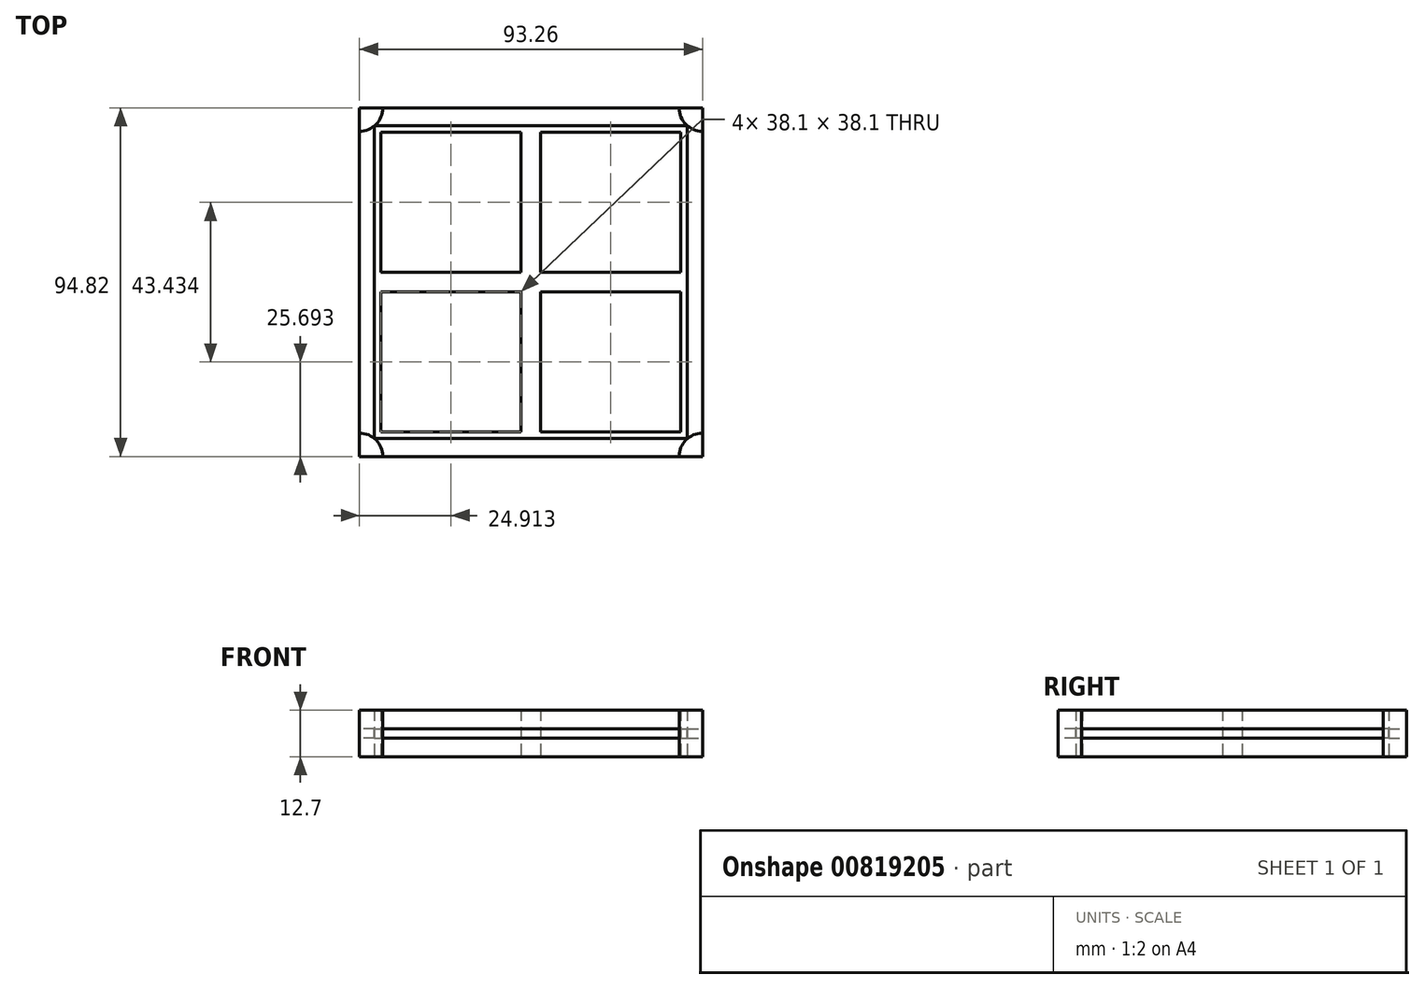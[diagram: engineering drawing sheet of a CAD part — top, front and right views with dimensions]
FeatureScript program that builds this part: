
annotation { "Feature Type Name" : "Feature", "Feature Type Description" : "" }
export const myFeature = defineFeature(function(context is Context, id is Id, definition is map)
    precondition{}
    {
        {
            var Q0;
            Q0=qCreatedBy(makeId("Top.planeOp"),FACE);
            var sketch = newSketch(context, id + "F0", { "sketchPlane" : qUnion([Q0])});
            skLineSegment(sketch, "E0.bottom", {"start": v(-42.55, 42.55) * mm, "end": v(42.55, 42.55) * mm});
            skLineSegment(sketch, "E0.top", {"start": v(-42.55, -42.55) * mm, "end": v(42.55, -42.55) * mm});
            skLineSegment(sketch, "E0.left", {"start": v(-42.55, 42.55) * mm, "end": v(-42.55, -42.55) * mm});
            skLineSegment(sketch, "E0.right", {"start": v(42.55, 42.55) * mm, "end": v(42.55, -42.55) * mm});
            skPoint(sketch, "E0.middle", {"position": v(0, 0) * mm});
            skCircle(sketch, "E1", {"center": v(46.63, -47.4) * mm, "radius": 6.35 * mm});
            skCircle(sketch, "E2", {"center": v(-46.63, -47.4) * mm, "radius": 6.35 * mm});
            skCircle(sketch, "E3", {"center": v(-46.63, 47.4) * mm, "radius": 6.35 * mm});
            skCircle(sketch, "E4", {"center": v(46.63, 47.4) * mm, "radius": 6.35 * mm});
            skLineSegment(sketch, "E5.bottom", {"start": v(-40.77, 40.77) * mm, "end": v(-2.67, 40.77) * mm});
            skLineSegment(sketch, "E5.top", {"start": v(-40.77, 2.67) * mm, "end": v(-2.67, 2.67) * mm});
            skLineSegment(sketch, "E5.left", {"start": v(-40.77, 40.77) * mm, "end": v(-40.77, 2.67) * mm});
            skLineSegment(sketch, "E5.right", {"start": v(-2.67, 40.77) * mm, "end": v(-2.67, 2.67) * mm});
            skLineSegment(sketch, "E6.bottom", {"start": v(2.67, 40.77) * mm, "end": v(40.77, 40.77) * mm});
            skLineSegment(sketch, "E6.top", {"start": v(2.67, 2.67) * mm, "end": v(40.77, 2.67) * mm});
            skLineSegment(sketch, "E6.left", {"start": v(2.67, 40.77) * mm, "end": v(2.67, 2.67) * mm});
            skLineSegment(sketch, "E6.right", {"start": v(40.77, 40.77) * mm, "end": v(40.77, 2.67) * mm});
            skLineSegment(sketch, "E7.bottom", {"start": v(-40.77, -2.67) * mm, "end": v(-2.67, -2.67) * mm});
            skLineSegment(sketch, "E7.top", {"start": v(-40.77, -40.77) * mm, "end": v(-2.67, -40.77) * mm});
            skLineSegment(sketch, "E7.left", {"start": v(-40.77, -2.67) * mm, "end": v(-40.77, -40.77) * mm});
            skLineSegment(sketch, "E7.right", {"start": v(-2.67, -2.67) * mm, "end": v(-2.67, -40.77) * mm});
            skLineSegment(sketch, "E8.bottom", {"start": v(2.67, -2.67) * mm, "end": v(40.77, -2.67) * mm});
            skLineSegment(sketch, "E8.top", {"start": v(2.67, -40.77) * mm, "end": v(40.77, -40.77) * mm});
            skLineSegment(sketch, "E8.left", {"start": v(2.67, -2.67) * mm, "end": v(2.67, -40.77) * mm});
            skLineSegment(sketch, "E8.right", {"start": v(40.77, -2.67) * mm, "end": v(40.77, -40.77) * mm});
            skLineSegment(sketch, "E9.bottom", {"start": v(40.77, 2.67) * mm, "end": v(40.77, 2.67) * mm});
            skLineSegment(sketch, "E9.top", {"start": v(40.77, -2.67) * mm, "end": v(40.77, -2.67) * mm});
            skLineSegment(sketch, "E9.left", {"start": v(40.77, 2.67) * mm, "end": v(40.77, -2.67) * mm});
            skLineSegment(sketch, "E9.right", {"start": v(40.77, 2.67) * mm, "end": v(40.77, -2.67) * mm});
            skLineSegment(sketch, "E10.bottom", {"start": v(-46.63, 47.4) * mm, "end": v(46.63, 47.4) * mm});
            skLineSegment(sketch, "E10.top", {"start": v(-46.63, -47.4) * mm, "end": v(46.63, -47.4) * mm});
            skLineSegment(sketch, "E10.left", {"start": v(-46.63, 47.4) * mm, "end": v(-46.63, -47.4) * mm});
            skLineSegment(sketch, "E10.right", {"start": v(46.63, 47.4) * mm, "end": v(46.63, -47.4) * mm});
            skSolve(sketch);
        }
        {
            var Q0;
            Q0=makeQuery(id+"F0.imprint","IMPRINT",FACE,{"disambiguationData":[TD([[makeQuery(id+"F0.imprint","IMPRINT",EDGE,{"derivedFrom":sQuery(id+"F0.wireOp",EDGE,"E4")}),1.0]])]});
            var Q1;
            Q1=makeQuery(id+"F0.imprint","IMPRINT",FACE,{"disambiguationData":[TD([[makeQuery(id+"F0.imprint","IMPRINT",EDGE,{"derivedFrom":sQuery(id+"F0.wireOp",EDGE,"E1")}),1.0]])]});
            var Q2;
            Q2=makeQuery(id+"F0.imprint","IMPRINT",FACE,{"disambiguationData":[TD([[makeQuery(id+"F0.imprint","IMPRINT",EDGE,{"derivedFrom":sQuery(id+"F0.wireOp",EDGE,"E3")}),1.0]])]});
            var Q3;
            Q3=makeQuery(id+"F0.imprint","IMPRINT",FACE,{"disambiguationData":[TD([[makeQuery(id+"F0.imprint","IMPRINT",EDGE,{"derivedFrom":sQuery(id+"F0.wireOp",EDGE,"E2")}),1.0]])]});
            extrude(context, id + "F1", {"entities" : qUnion([Q0, Q1, Q2, Q3]), "endBound" : BoundingType.SYMMETRIC, "depth" : 12.7 * mm, "offsetDistance" : 25.4 * mm});
        }
        {
            var Q0;
            Q0=makeQuery(id+"F0.imprint","IMPRINT",FACE,{"disambiguationData":[TD([[makeQuery(id+"F0.imprint","IMPRINT",EDGE,{"derivedFrom":sQuery(id+"F0.wireOp",EDGE,"E0.bottom")}),-1.0]])]});
            extrude(context, id + "F2", {"entities" : qUnion([Q0]), "endBound" : BoundingType.SYMMETRIC, "depth" : 12.7 * mm, "hasOffset" : true, "offsetDistance" : 25.4 * mm, "hasSecondDirection" : true, "secondDirectionOppositeDirection" : false, "secondDirectionDepth" : 25.4 * mm});
        }
        {
            var Q0;
            {var subQ0=sQuery(id+"F0.wireOp",EDGE,"E0.left");Q0=makeQuery(id+"F0.imprint","IMPRINT",FACE,{"disambiguationData":[TD([[makeQuery(id+"F0.imprint","IMPRINT",EDGE,{"derivedFrom":subQ0}),-1.0]])]});}
            var Q1;
            {var subQ0=sQuery(id+"F0.wireOp",EDGE,"E0.bottom");Q1=makeQuery(id+"F0.imprint","IMPRINT",FACE,{"disambiguationData":[TD([[makeQuery(id+"F0.imprint","IMPRINT",EDGE,{"derivedFrom":subQ0}),1.0]])]});}
            var Q2;
            {var subQ0=sQuery(id+"F0.wireOp",EDGE,"E0.right");Q2=makeQuery(id+"F0.imprint","IMPRINT",FACE,{"disambiguationData":[TD([[makeQuery(id+"F0.imprint","IMPRINT",EDGE,{"derivedFrom":subQ0}),1.0]])]});}
            var Q3;
            {var subQ0=sQuery(id+"F0.wireOp",EDGE,"E0.top");Q3=makeQuery(id+"F0.imprint","IMPRINT",FACE,{"disambiguationData":[TD([[makeQuery(id+"F0.imprint","IMPRINT",EDGE,{"derivedFrom":subQ0}),-1.0]])]});}
            extrude(context, id + "F3", {"entities" : qUnion([Q0, Q1, Q2, Q3]), "endBound" : BoundingType.SYMMETRIC, "oppositeDirection" : true, "depth" : 2.54 * mm, "offsetDistance" : 25.4 * mm});
        }
    });
